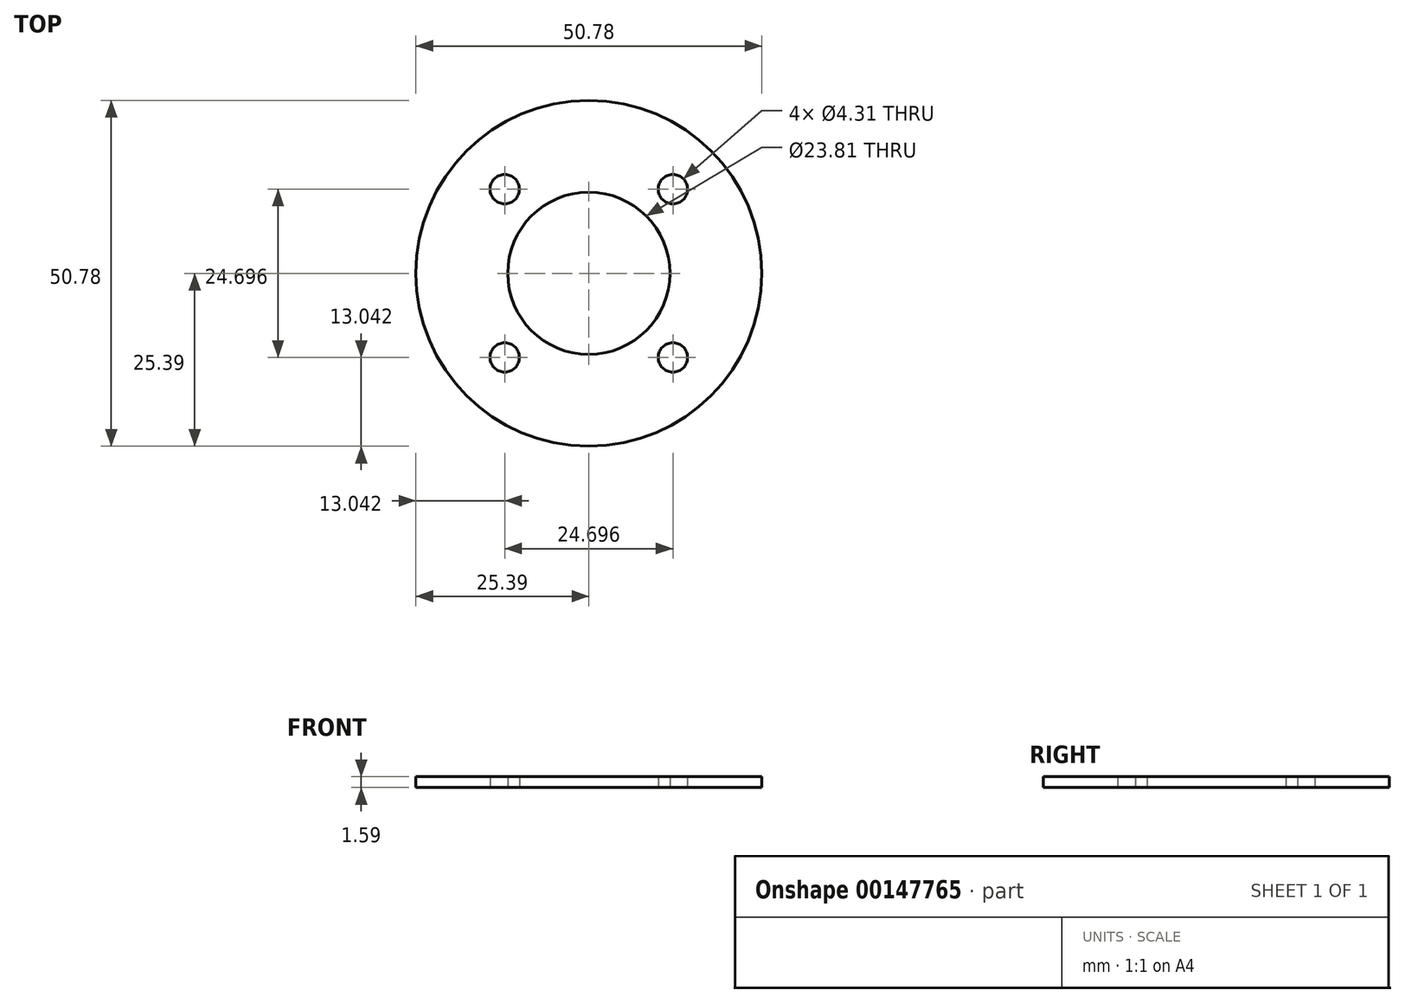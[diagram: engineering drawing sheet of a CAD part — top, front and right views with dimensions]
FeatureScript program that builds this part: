
annotation { "Feature Type Name" : "Feature", "Feature Type Description" : "" }
export const myFeature = defineFeature(function(context is Context, id is Id, definition is map)
    precondition{}
    {
        {
            var Q0;
            Q0=qCreatedBy(makeId("Top.planeOp"),FACE);
            var sketch = newSketch(context, id + "F0", { "sketchPlane" : qUnion([Q0])});
            skCircle(sketch, "E0", {"center": v(0, 0) * mm, "radius": 25.4 * mm});
            skCircle(sketch, "E1", {"center": v(0, 0) * mm, "radius": 11.9 * mm});
            skLineSegment(sketch, "E2.bottom", {"start": v(-12.35, 12.35) * mm, "end": v(12.35, 12.35) * mm, "construction": true});
            skLineSegment(sketch, "E2.top", {"start": v(-12.35, -12.35) * mm, "end": v(12.35, -12.35) * mm, "construction": true});
            skLineSegment(sketch, "E2.left", {"start": v(-12.35, 12.35) * mm, "end": v(-12.35, -12.35) * mm, "construction": true});
            skLineSegment(sketch, "E2.right", {"start": v(12.35, 12.35) * mm, "end": v(12.35, -12.35) * mm, "construction": true});
            skCircle(sketch, "E3", {"center": v(-12.35, 12.35) * mm, "radius": 5.56 * mm, "construction": true});
            skCircle(sketch, "E4", {"center": v(12.35, 12.35) * mm, "radius": 2.15 * mm});
            skCircle(sketch, "E5", {"center": v(-12.35, 12.35) * mm, "radius": 2.15 * mm});
            skCircle(sketch, "E6", {"center": v(-12.35, -12.35) * mm, "radius": 2.15 * mm});
            skCircle(sketch, "E7", {"center": v(12.35, -12.35) * mm, "radius": 2.15 * mm});
            skSolve(sketch);
        }
        {
            var Q0;
            Q0=qSketchRegion(id+"F0",true);
            extrude(context, id + "F1", {"entities" : qUnion([Q0]), "depth" : 1.59 * mm});
        }
    });
